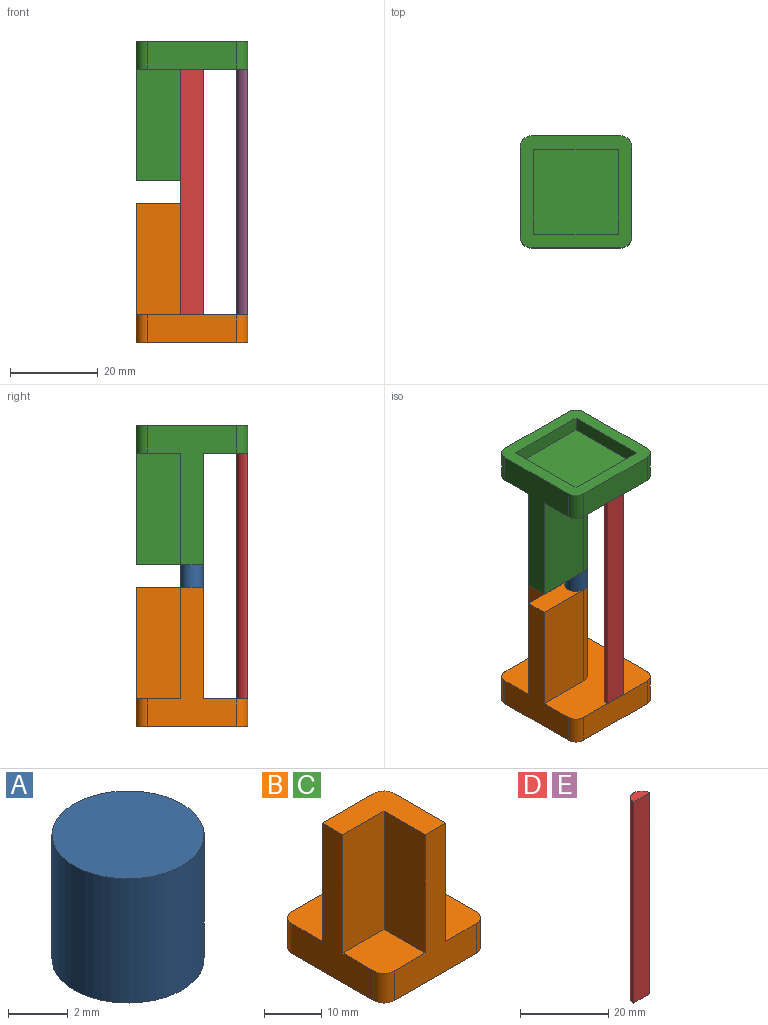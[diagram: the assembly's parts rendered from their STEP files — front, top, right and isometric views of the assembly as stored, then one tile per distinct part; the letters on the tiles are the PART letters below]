
ASSEMBLY  parts=5 mates=6
PART A: 3 faces, bbox 5.1x5.1x5.1 mm
  f0: cylinder r=2.54mm len=5.08mm, axis (0,0,-1), area 81.1mm2, adj f1,f2
  f1: plane 5.08x5.08mm, normal (0,0,1), area 20.3mm2, adj f0
  f2: plane 5.08x5.08mm, normal (0,0,-1), area 20.3mm2, adj f0
PART B: 22 faces, bbox 25.4x25.4x31.8 mm
  f0: plane 10.16x10.16mm, normal (0,0,1), area 101.8mm2, adj f4,f5,f9,f16,f19
  f1: plane 25.4x25.4mm, normal (0,0,1), area 410.1mm2, adj f2,f3,f4,f5,f7,f8,f10,f17
  f2: plane 20.32x6.35mm, normal (1,0,0), area 129mm2, adj f1,f6,f7,f10
  f3: plane 20.32x6.35mm, normal (0,1,0), area 129mm2, adj f1,f6,f7,f8
  f4: plane 31.75x20.32mm, normal (-1,0,0), area 258.1mm2, adj f0,f1,f6,f8,f9,f18,f19,f20
  f5: plane 31.75x20.32mm, normal (0,-1,0), area 258.1mm2, adj f0,f1,f6,f9,f10,f16,f17,f20
  f6: plane 25.4x25.4mm, normal (0,0,-1), area 267mm2, adj f2,f3,f4,f5,f7,f8,f9,f10
  f7: cylinder r=2.54mm len=6.35mm, axis (0,0,1), area 25.3mm2, adj f1,f2,f3,f6
  f8: cylinder r=2.54mm len=6.35mm, axis (0,0,-1), area 25.3mm2, adj f1,f3,f4,f6
  f9: cylinder r=2.54mm len=6.35mm, axis (0,0,1), area 25.3mm2, adj f0,f4,f5,f6
  f10: cylinder r=2.54mm len=6.35mm, axis (0,0,-1), area 25.3mm2, adj f1,f2,f5,f6
  f11: plane 19.3x3.3mm, normal (-1,0,0), area 63.7mm2, adj f6,f12,f14,f15
  f12: plane 19.3x3.3mm, normal (0,-1,0), area 63.7mm2, adj f6,f11,f13,f15
  f13: plane 19.3x3.3mm, normal (1,0,0), area 63.7mm2, adj f6,f12,f14,f15
  f14: plane 19.3x3.3mm, normal (0,1,0), area 63.7mm2, adj f6,f11,f13,f15
  f15: plane 19.3x19.3mm, normal (0,0,-1), area 372.6mm2, adj f11,f12,f13,f14
  f16: plane 25.4x10.16mm, normal (-1,0,0), area 258.1mm2, adj f0,f5,f19,f20
  f17: plane 25.4x12.7mm, normal (1,0,0), area 322.6mm2, adj f1,f5,f20,f21
  f18: plane 25.4x12.7mm, normal (0,1,0), area 322.6mm2, adj f1,f4,f20,f21
  f19: plane 25.4x10.16mm, normal (0,-1,0), area 258.1mm2, adj f0,f4,f16,f20
  f20: plane 15.24x15.24mm, normal (0,0,1), area 127.6mm2, adj f4,f5,f16,f17,f18,f19,f21
  f21: cylinder r=2.54mm len=25.4mm, axis (0,0,-1), area 101.3mm2, adj f1,f17,f18,f20
PART C: same geometry as B
PART D: 4 faces, bbox 5.1x2.5x55.9 mm
  f0: plane 55.88x5.08mm, normal (0,-1,0), area 283.9mm2, adj f1,f2,f3
  f1: cylinder r=2.54mm len=55.88mm, axis (0,0,-1), area 445.9mm2, adj f0,f2,f3
  f2: plane 5.08x2.54mm, normal (0,0,1), area 10.1mm2, adj f0,f1
  f3: plane 5.08x2.54mm, normal (0,0,-1), area 10.1mm2, adj f0,f1
PART E: same geometry as D
PLACE A t=(54.46,7.94,-15.63)mm
PLACE B rot(axis=(0,0,-1),90deg) t=(24.4,128.13,-47.38)mm
PLACE C rot(axis=(1,0,0),180deg) t=(-89.9,13.83,21.2)mm
PLACE D t=(72.88,16.94,-41.03)mm
PLACE E rot(axis=(0,0,1),90deg) t=(21.29,62.3,-41.03)mm
MATE fastened B.f21 <-> A.f0  axis (0,0,1) through (24.4,13.83,-15.63)mm
MATE planar E.f0 <-> C.f2  axis (1,0,0) through (37.1,13.83,-13.09)mm
MATE fastened A.f0 <-> C.f21  axis (0,0,1) through (24.4,13.83,-10.55)mm
MATE fastened D.f1 <-> C.f1  axis (0,0,1) through (24.4,1.13,14.85)mm
MATE fastened C.f1 <-> E.f1  axis (0,0,-1) through (37.1,13.83,14.85)mm
MATE planar D.f0 <-> C.f3  axis (0,-1,0) through (24.4,1.13,-13.09)mm
